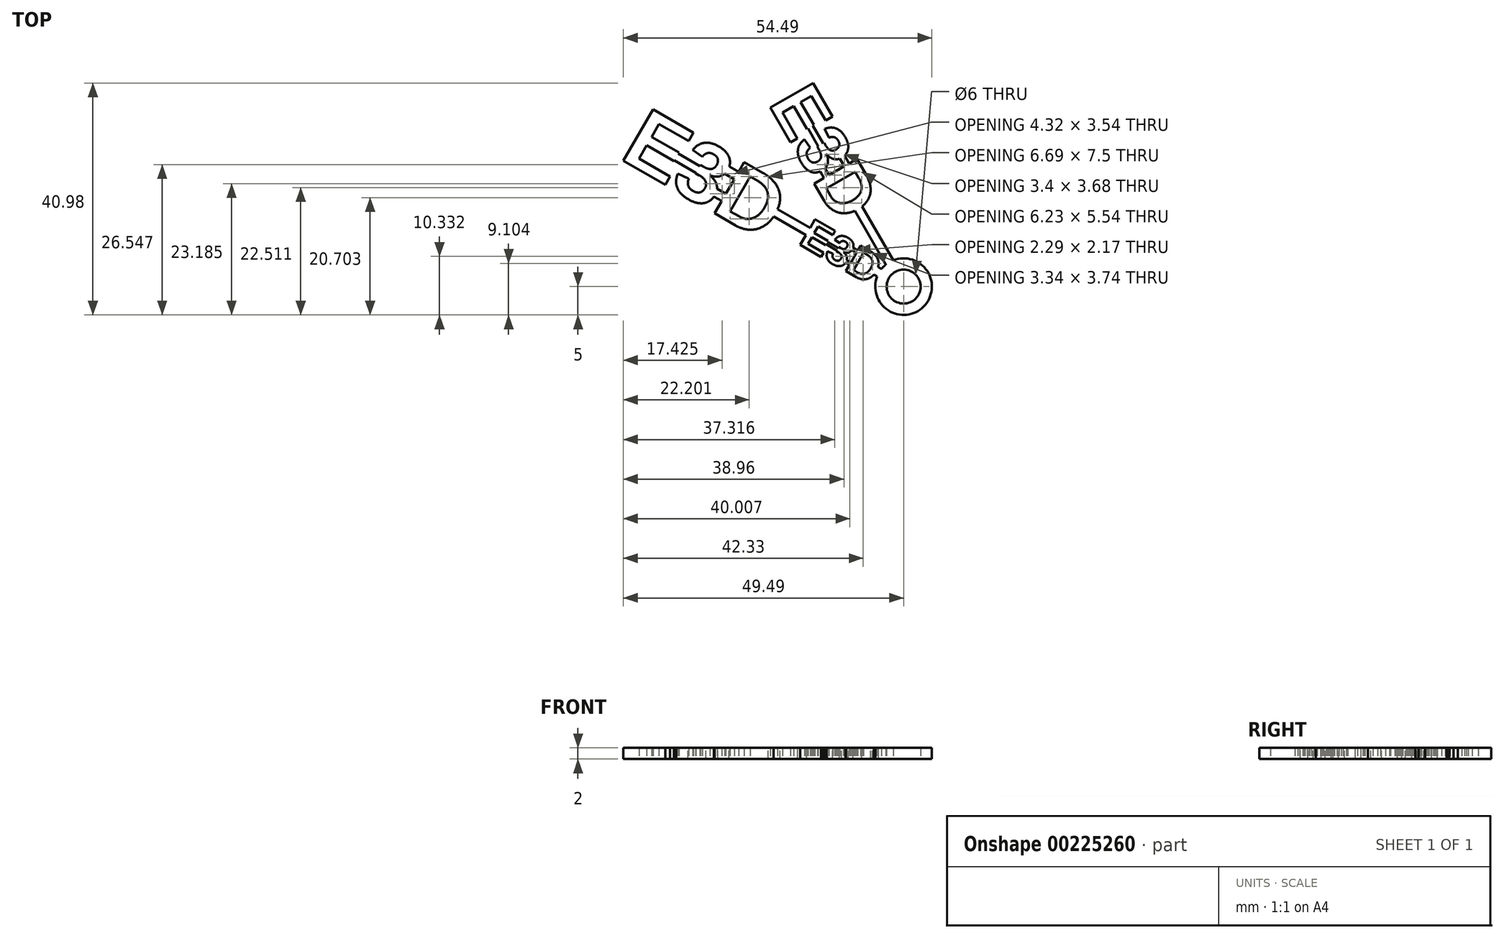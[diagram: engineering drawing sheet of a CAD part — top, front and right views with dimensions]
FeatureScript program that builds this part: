
annotation { "Feature Type Name" : "Feature", "Feature Type Description" : "" }
export const myFeature = defineFeature(function(context is Context, id is Id, definition is map)
    precondition{}
    {
        {
            var Q0;
            Q0=qCreatedBy(makeId("Top.planeOp"),FACE);
            var sketch = newSketch(context, id + "F0", { "sketchPlane" : qUnion([Q0])});
            skLineSegment(sketch, "E0", {"start": v(0, 0) * mm, "end": v(0, 9.52) * mm, "construction": true});
            skLineSegment(sketch, "E1", {"start": v(0, 0) * mm, "end": v(-8.36, 4.82) * mm, "construction": true});
            skText(sketch, "E2", { "text": "E3D", "fontName": "Arimo-Bold.ttf"});
            skPoint(sketch, "E3", {"position": v(-4.33, 2.5) * mm});
            skLineSegment(sketch, "E4", {"start": v(0, 0) * mm, "end": v(-11.46, 19.85) * mm, "construction": true});
            skPoint(sketch, "E5", {"position": v(-7.5, 13) * mm});
            skText(sketch, "E6", { "text": "E3D", "fontName": "Arimo-Bold.ttf"});
            skPoint(sketch, "E7", {"position": v(-21.65, 12.5) * mm});
            skLineSegment(sketch, "E8.bottom", {"start": v(-31.69, 21.73) * mm, "end": v(-28.55, 19.92) * mm});
            skLineSegment(sketch, "E8.top", {"start": v(-32.44, 20.43) * mm, "end": v(-29.3, 18.62) * mm});
            skLineSegment(sketch, "E9.bottom", {"start": v(-40.05, 23.67) * mm, "end": v(-35.83, 21.24) * mm});
            skLineSegment(sketch, "E9.top", {"start": v(-40.76, 22.45) * mm, "end": v(-36.54, 20.02) * mm});
            skLineSegment(sketch, "E10.MirrorCS", {"start": v(-34.66, 16.58) * mm, "end": v(-31.52, 14.76) * mm});
            skLineSegment(sketch, "E11.MirrorCS", {"start": v(-33.91, 17.88) * mm, "end": v(-30.77, 16.06) * mm});
            skText(sketch, "E12", { "text": "E3D", "fontName": "Arimo-Bold.ttf"});
            skLineSegment(sketch, "E13.bottom", {"start": v(-10.68, 23.63) * mm, "end": v(-8.87, 20.49) * mm});
            skLineSegment(sketch, "E13.top", {"start": v(-11.55, 23.13) * mm, "end": v(-9.74, 19.99) * mm});
            skLineSegment(sketch, "E14.bottom", {"start": v(-16.67, 29.6) * mm, "end": v(-13.77, 24.57) * mm});
            skLineSegment(sketch, "E14.top", {"start": v(-17.45, 28.96) * mm, "end": v(-14.55, 23.93) * mm});
            skLineSegment(sketch, "E15.MirrorCS", {"start": v(-14.26, 21.57) * mm, "end": v(-12.44, 18.43) * mm});
            skLineSegment(sketch, "E16.MirrorCS", {"start": v(-15.12, 21.07) * mm, "end": v(-13.3, 17.93) * mm});
            skLineSegment(sketch, "E17", {"start": v(-13.76, 8.1) * mm, "end": v(-11.44, 6.76) * mm});
            skLineSegment(sketch, "E18", {"start": v(-11.66, 6.31) * mm, "end": v(-14, 7.66) * mm});
            skLineSegment(sketch, "E19", {"start": v(-9.1, 6.97) * mm, "end": v(-7.67, 6.15) * mm});
            skLineSegment(sketch, "E20", {"start": v(-7.92, 5.71) * mm, "end": v(-9.3, 6.51) * mm});
            skLineSegment(sketch, "E21.MirrorCS", {"start": v(-8.91, 4) * mm, "end": v(-10.3, 4.8) * mm});
            skLineSegment(sketch, "E22.MirrorCS", {"start": v(-10.58, 4.4) * mm, "end": v(-9.16, 3.57) * mm});
            skLineSegment(sketch, "E23", {"start": v(-22.69, 13.95) * mm, "end": v(-16.18, 10.2) * mm});
            skLineSegment(sketch, "E24", {"start": v(-16.18, 10.2) * mm, "end": v(-16.93, 8.9) * mm});
            skLineSegment(sketch, "E25", {"start": v(-16.93, 8.9) * mm, "end": v(-23.48, 12.67) * mm});
            skCircle(sketch, "E26", {"center": v(0, 0) * mm, "radius": 5 * mm});
            skCircle(sketch, "E27", {"center": v(0, 0) * mm, "radius": 3 * mm});
            skLineSegment(sketch, "E28", {"start": v(-4.92, 3.7) * mm, "end": v(-3.24, 2.74) * mm});
            skLineSegment(sketch, "E29.MirrorCS", {"start": v(-5.67, 2.4) * mm, "end": v(-4, 1.44) * mm});
            skLineSegment(sketch, "E30", {"start": v(-7.57, 14.6) * mm, "end": v(-1.22, 3.62) * mm});
            skLineSegment(sketch, "E31.MirrorCS", {"start": v(-8.87, 13.86) * mm, "end": v(-2.52, 2.87) * mm});
            const initialGuessF0  = {"E2": [-0.01869, 0.00763, 0.86603, -0.5, 0.00547], "E6": [-0.05037, 0.02276, 0.86603, -0.5, 0.01095], "E12": [-0.02395, 0.03236, 0.5, -0.86603, 0.00912]};
            skSetInitialGuess(sketch, initialGuessF0);
            skSolve(sketch);
        }
        {
            var Q0;
            Q0 = qSketchRegion(id + "F0", true);
            extrude(context, id + "F1", {"entities" : qUnion([Q0]), "depth" : 2 * mm});
        }
    });
